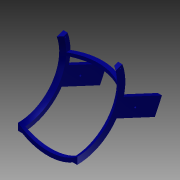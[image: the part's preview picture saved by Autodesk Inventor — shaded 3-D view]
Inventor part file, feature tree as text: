
AUTODESK INVENTOR PART (.ipt)
format: ipt  version: 2014 (Build 180170000, 170)  size: 204,288 bytes
history: native  units: in
note: dims shown in document units (in); Inventor stores cm internally (conversion verified against a paired STEP export)
features: sketch x8, revolve x3, hole x3, extrude x3, plane x2, projected_geometry x2
ambient origin geometry x8: Origin, YZ Plane, XZ Plane, XY Plane, X Axis, Y Axis, Z Axis, Center Point
bodies: Solid1 (feature_tree)
feature tree (21):
  revolve  "Revolution1"  [1 undecoded]
  revolve  "Revolution2"  [1 undecoded]
  plane  "Work Plane1"
  plane  "Work Plane2"
  revolve  "Revolution4"  [1 undecoded]
  sketch  "Sketch9"  dims[d10=12.0in d44=12.0in]
  hole  "Hole3"  [1 undecoded]
  hole  "Hole4"  [1 undecoded]
  extrude  "Extrusion3"  Depth=3.0in
  extrude  "Extrusion4"  Depth=3.0in
  hole  "Hole5"  [1 undecoded]
  extrude  "Extrusion5"  Depth=3.0in
  sketch  "Sketch1"  dims[d1=12.0in d3=12.0in]
  sketch  "Sketch2"  dims[d5=0.7559in d6=12.0in]
  projected_geometry  "Projected Loop1"
  sketch  "Sketch8"  dims[d7=12.0in d9=0.0275in]
  sketch  "Sketch10"  dims[d45=12.0in d46=0.0275in]
  sketch  "Sketch11"  dims[d47=0.5in]
  sketch  "Sketch12"  dims[d48=0.25in d49=0.75in d50=0.375in d51=0.25in d52=0.5635in d53=1.0in d54=0.8108in]
  sketch  "Sketch13"  dims[d55=0.25in d56=0.75in d57=0.375in d58=0.25in d59=0.5635in d60=1.0in d61=0.8108in d65=10.0in d66=0.1718in d67=10.0in d68=0.1718in d69=1.0in d70=0.0in d71=1.0in d72=0.0in d73=6.0in d74=0.5in d75=0.75in d76=0.375in d77=0.25in d78=0.5635in d79=1.0in d80=0.8108in d81=2.0in d82=3.0in d83=0.72in d84=0.0in]
  projected_geometry  "Project Cut Edges2"
note: 6 required parameter values undecoded (feature->parameter linkage not recoverable at this tier; creation-order binding heuristic only, values carry confidence <= 0.55)